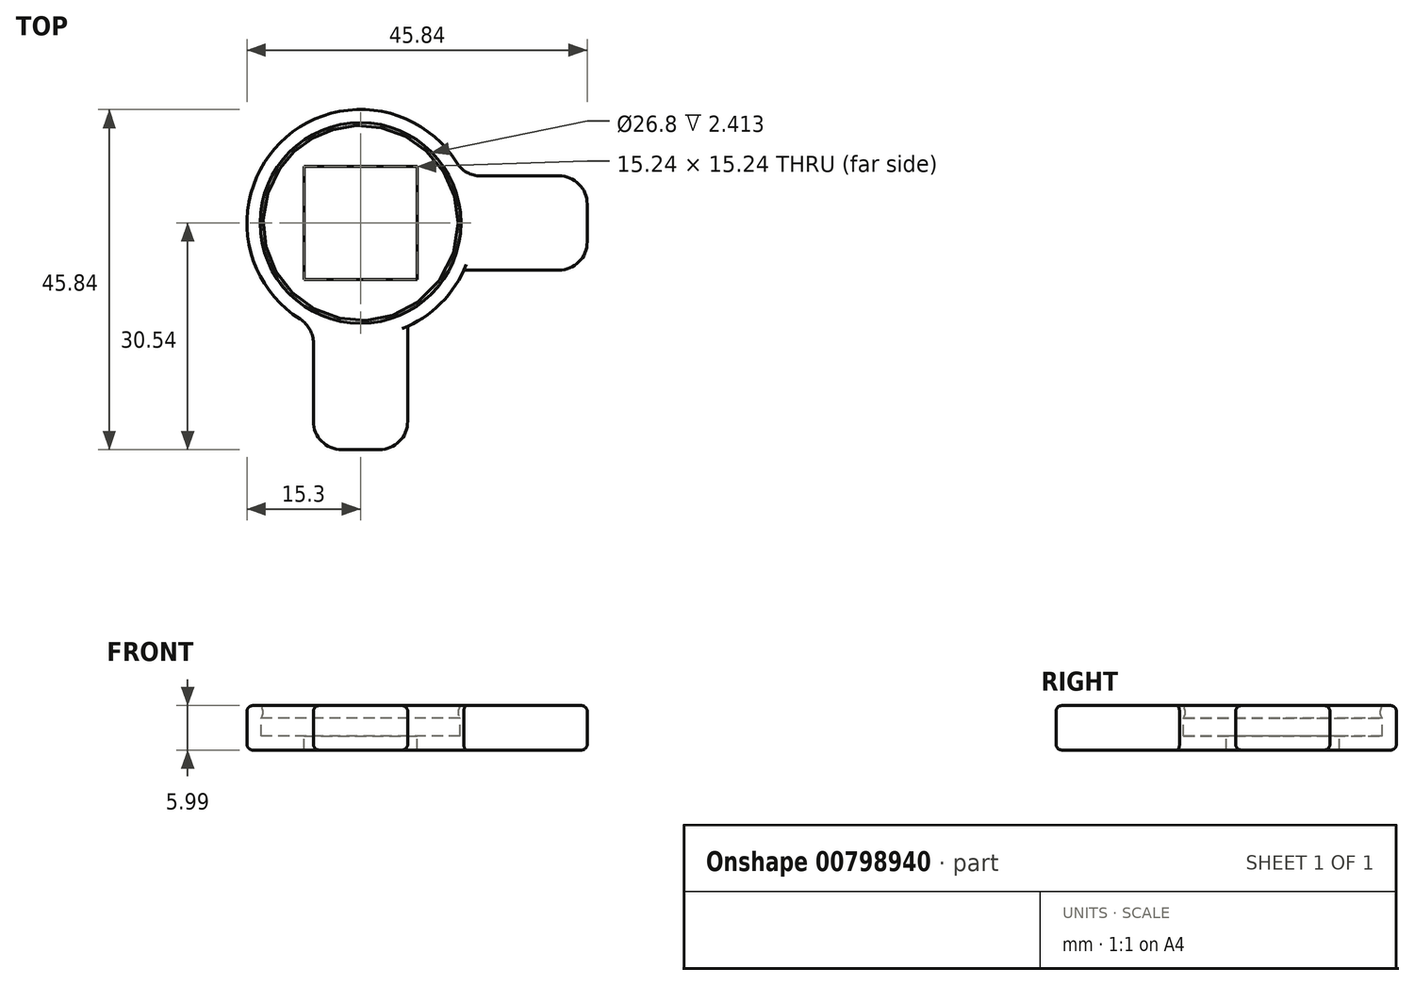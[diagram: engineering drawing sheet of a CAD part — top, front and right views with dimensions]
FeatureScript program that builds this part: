
annotation { "Feature Type Name" : "Feature", "Feature Type Description" : "" }
export const myFeature = defineFeature(function(context is Context, id is Id, definition is map)
    precondition{}
    {
        {
            var Q0;
            Q0=qCreatedBy(makeId("Front.planeOp"),FACE);
            var sketch = newSketch(context, id + "F0", { "sketchPlane" : qUnion([Q0])});
            skLineSegment(sketch, "E0", {"start": v(15.3, 4.17) * mm, "end": v(15.3, 0) * mm});
            skLineSegment(sketch, "E1", {"start": v(15.3, 0) * mm, "end": v(0, 0) * mm});
            skArc(sketch, "E2", {"start": v(15.3, 4.17) * mm, "mid": v(13.5, 4.2) * mm, "end": v(13.53, 5.99) * mm});
            skLineSegment(sketch, "E3", {"start": v(0, 10.9) * mm, "end": v(0, -2.45) * mm, "construction": true});
            skLineSegment(sketch, "E4", {"start": v(0, 0) * mm, "end": v(0, 1.9) * mm});
            skLineSegment(sketch, "E5", {"start": v(0, 1.9) * mm, "end": v(13.4, 1.9) * mm});
            skLineSegment(sketch, "E6", {"start": v(13.4, 1.9) * mm, "end": v(13.4, 4.32) * mm});
            skLineSegment(sketch, "E7", {"start": v(15.3, 4.17) * mm, "end": v(15.3, 5.99) * mm});
            skLineSegment(sketch, "E8", {"start": v(15.3, 5.99) * mm, "end": v(13.53, 5.99) * mm});
            skSolve(sketch);
        }
        {
            var Q0;
            Q0=qSketchRegion(id+"F0",true);
            var Q1;
            Q1=sQuery(id+"F0.wireOp",EDGE,"E3");
            revolve(context, id + "F1", {"surfaceOperationType" : NewSurfaceOperationType.NEW, "entities" : qUnion([Q0]), "axis" : qUnion([Q1]), "revolveType" : RevolveType.FULL});
        }
        {
            var Q0;
            Q0=makeQuery(id+"F1.opRevolve","SWEPT_FACE",FACE,{"disambiguationData":[OSD([sQuery(id+"F0.wireOp",EDGE,"E8")])]});
            var sketch = newSketch(context, id + "F2", { "sketchPlane" : qUnion([Q0])});
            skLineSegment(sketch, "E9.bottom", {"start": v(30.54, 6.35) * mm, "end": v(13.92, 6.35) * mm});
            skLineSegment(sketch, "E9.top", {"start": v(30.54, -6.35) * mm, "end": v(13.92, -6.35) * mm});
            skLineSegment(sketch, "E9.left", {"start": v(30.54, 6.35) * mm, "end": v(30.54, -6.35) * mm});
            skLineSegment(sketch, "E10.bottom", {"start": v(6.35, -30.54) * mm, "end": v(-6.35, -30.54) * mm});
            skLineSegment(sketch, "E10.left", {"start": v(6.35, -30.54) * mm, "end": v(6.35, -13.92) * mm});
            skLineSegment(sketch, "E10.right", {"start": v(-6.35, -30.54) * mm, "end": v(-6.35, -13.92) * mm});
            skArc(sketch, "E11.0", {"start": v(-6.35, -13.92) * mm, "mid": v(0, -15.3) * mm, "end": v(6.35, -13.92) * mm});
            skArc(sketch, "E12.trimOffspring", {"start": v(13.92, -6.35) * mm, "mid": v(15.3, 0) * mm, "end": v(13.92, 6.35) * mm});
            skSolve(sketch);
        }
        {
            var Q0;
            Q0=qSketchRegion(id+"F2",true);
            var Q1;
            Q1=makeQuery(id+"F1.opRevolve","SWEPT_FACE",FACE,{"disambiguationData":[OSD([sQuery(id+"F0.wireOp",EDGE,"E1")])]});
            extrude(context, id + "F3", {"entities" : qUnion([Q0]), "operationType" : NewBodyOperationType.ADD, "endBound" : BoundingType.UP_TO_SURFACE, "oppositeDirection" : true, "depth" : 25.4 * mm, "endBoundEntityFace" : qUnion([Q1]), "offsetDistance" : 25.4 * mm});
        }
        {
            var Q0;
            Q0=makeQuery(id+"F3.opExtrude","SWEPT_EDGE",EDGE,{"disambiguationData":[OSD([sQuery(id+"F2.wireOp",EDGE,"E10.bottom"),sQuery(id+"F2.wireOp",EDGE,"E10.right")])]});
            var Q1;
            Q1=makeQuery(id+"F3.opExtrude","SWEPT_EDGE",EDGE,{"disambiguationData":[OSD([sQuery(id+"F0.wireOp",EDGE,"E7"),sQuery(id+"F0.wireOp",EDGE,"E8"),sQuery(id+"F2.wireOp",EDGE,"E10.right"),sQuery(id+"F2.wireOp",EDGE,"E11.0")])]});
            var Q2;
            Q2=makeQuery(id+"F3.opExtrude","SWEPT_EDGE",EDGE,{"disambiguationData":[OSD([sQuery(id+"F2.wireOp",EDGE,"E10.bottom"),sQuery(id+"F2.wireOp",EDGE,"E10.left")])]});
            var Q3;
            Q3=makeQuery(id+"F3.opExtrude","SWEPT_EDGE",EDGE,{"disambiguationData":[OSD([sQuery(id+"F0.wireOp",EDGE,"E7"),sQuery(id+"F0.wireOp",EDGE,"E8"),sQuery(id+"F2.wireOp",EDGE,"E10.left"),sQuery(id+"F2.wireOp",EDGE,"E11.0")])]});
            var Q4;
            Q4=makeQuery(id+"F3.opExtrude","SWEPT_EDGE",EDGE,{"disambiguationData":[OSD([sQuery(id+"F0.wireOp",EDGE,"E7"),sQuery(id+"F0.wireOp",EDGE,"E8"),sQuery(id+"F2.wireOp",EDGE,"E9.top"),sQuery(id+"F2.wireOp",EDGE,"E12.trimOffspring")])]});
            var Q5;
            Q5=makeQuery(id+"F3.opExtrude","SWEPT_EDGE",EDGE,{"disambiguationData":[OSD([sQuery(id+"F2.wireOp",EDGE,"E9.top"),sQuery(id+"F2.wireOp",EDGE,"E9.left")])]});
            var Q6;
            Q6=makeQuery(id+"F3.opExtrude","SWEPT_EDGE",EDGE,{"disambiguationData":[OSD([sQuery(id+"F2.wireOp",EDGE,"E9.bottom"),sQuery(id+"F2.wireOp",EDGE,"E9.left")])]});
            var Q7;
            Q7=makeQuery(id+"F3.opExtrude","SWEPT_EDGE",EDGE,{"disambiguationData":[OSD([sQuery(id+"F0.wireOp",EDGE,"E7"),sQuery(id+"F0.wireOp",EDGE,"E8"),sQuery(id+"F2.wireOp",EDGE,"E9.bottom"),sQuery(id+"F2.wireOp",EDGE,"E12.trimOffspring")])]});
            fillet(context, id + "F4", {"entities" : qUnion([Q0, Q1, Q2, Q3, Q4, Q5, Q6, Q7]), "radius" : 3.8 * mm, "tangentPropagation" : true, "allowEdgeOverflow" : false});
        }
        {
            var Q0;
            Q0=makeQuery(id+"F3.opExtrude","CAP_EDGE",EDGE,{"disambiguationData":[OSD([sQuery(id+"F2.wireOp",EDGE,"E10.bottom")])],"isStart":true});
            var Q1;
            Q1=makeQuery(id+"F3.opExtrude","CAP_EDGE",EDGE,{"disambiguationData":[OSD([sQuery(id+"F2.wireOp",EDGE,"E10.bottom")])],"isStart":false});
            fillet(context, id + "F5", {"entities" : qUnion([Q0, Q1]), "radius" : 0.76 * mm, "tangentPropagation" : true, "allowEdgeOverflow" : false});
        }
        {
            var Q0;
            Q0=makeQuery(id+"F1.opRevolve","SWEPT_FACE",FACE,{"disambiguationData":[OSD([sQuery(id+"F0.wireOp",EDGE,"E5")])]});
            var sketch = newSketch(context, id + "F6", { "sketchPlane" : qUnion([Q0])});
            skLineSegment(sketch, "E13.bottom", {"start": v(-7.62, 7.62) * mm, "end": v(7.62, 7.62) * mm});
            skLineSegment(sketch, "E13.top", {"start": v(-7.62, -7.62) * mm, "end": v(7.62, -7.62) * mm});
            skLineSegment(sketch, "E13.left", {"start": v(-7.62, 7.62) * mm, "end": v(-7.62, -7.62) * mm});
            skLineSegment(sketch, "E13.right", {"start": v(7.62, 7.62) * mm, "end": v(7.62, -7.62) * mm});
            skSolve(sketch);
        }
        {
            var Q0;
            Q0 = qSketchRegion(id + "F6", true);
            extrude(context, id + "F7", {"entities" : qUnion([Q0]), "operationType" : NewBodyOperationType.REMOVE, "oppositeDirection" : true, "depth" : 25.4 * mm, "offsetDistance" : 25.4 * mm});
        }
    });
